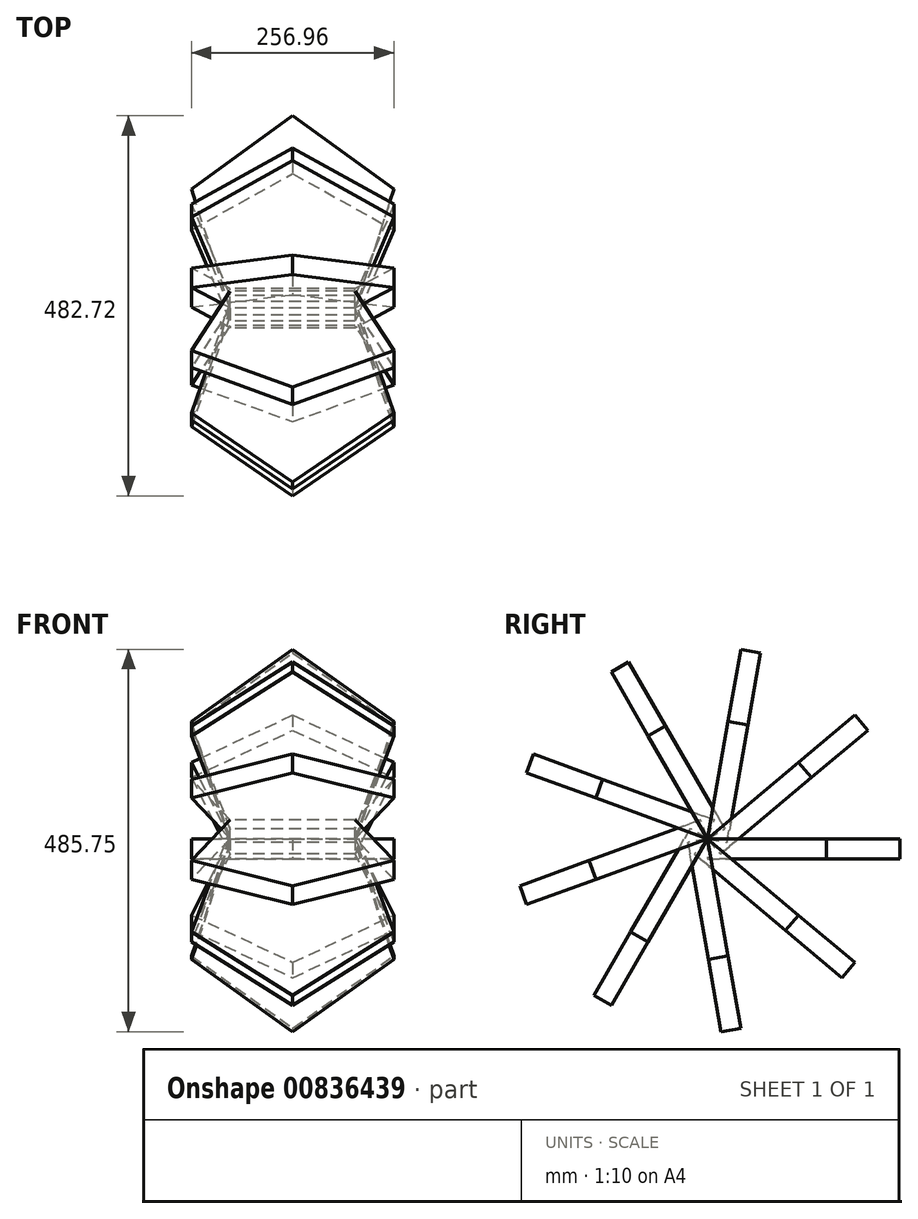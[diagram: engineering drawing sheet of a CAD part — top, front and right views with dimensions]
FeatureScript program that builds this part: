
annotation { "Feature Type Name" : "Feature", "Feature Type Description" : "" }
export const myFeature = defineFeature(function(context is Context, id is Id, definition is map)
    precondition{}
    {
        {
            var Q0;
            Q0=qCreatedBy(makeId("Top.planeOp"),FACE);
            var sketch = newSketch(context, id + "F0", { "sketchPlane" : qUnion([Q0])});
            skCircle(sketch, "E0.cCircle", {"center": v(0, 0) * mm, "radius": 109.3 * mm, "construction": true});
            skLineSegment(sketch, "E0.0", {"start": v(128.48, 41.75) * mm, "end": v(79.4, -109.3) * mm});
            skLineSegment(sketch, "E0.1", {"start": v(79.4, -109.3) * mm, "end": v(-79.4, -109.3) * mm});
            skLineSegment(sketch, "E0.2", {"start": v(-79.4, -109.3) * mm, "end": v(-128.48, 41.75) * mm});
            skLineSegment(sketch, "E0.3", {"start": v(-128.48, 41.75) * mm, "end": v(0, 135.1) * mm});
            skLineSegment(sketch, "E0.4", {"start": v(0, 135.1) * mm, "end": v(128.48, 41.75) * mm});
            skPoint(sketch, "E0.0.midPoint", {"position": v(103.94, -33.77) * mm});
            skSolve(sketch);
        }
        {
            var Q0;
            Q0 = qSketchRegion(id + "F0", true);
            extrude(context, id + "F1", {"entities" : qUnion([Q0]), "depth" : 25.4 * mm, "offsetDistance" : 25.4 * mm});
        }
        {
            var Q0;
            Q0=makeQuery(id+"F1.opExtrude","SWEPT_BODY",BODY,{"disambiguationData":[OSD([sQuery(id+"F0.wireOp",EDGE,"E0.0"),sQuery(id+"F0.wireOp",EDGE,"E0.1"),sQuery(id+"F0.wireOp",EDGE,"E0.2"),sQuery(id+"F0.wireOp",EDGE,"E0.3"),sQuery(id+"F0.wireOp",EDGE,"E0.4")])]});
            var Q1;
            Q1=makeQuery(id+"F1.opExtrude","CAP_EDGE",EDGE,{"disambiguationData":[OSD([sQuery(id+"F0.wireOp",EDGE,"E0.1")])],"isStart":false});
            circularPattern(context, id + "F2", {"entities" : qUnion([Q0]), "axis" : qUnion([Q1]), "angle" : 360 * degree, "instanceCount" : 9, "equalSpace" : true});
        }
    });
